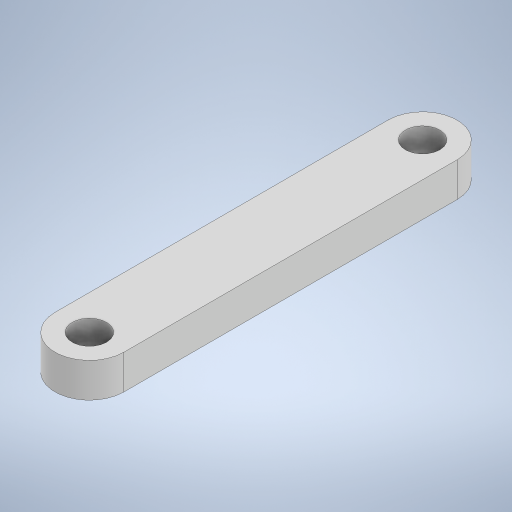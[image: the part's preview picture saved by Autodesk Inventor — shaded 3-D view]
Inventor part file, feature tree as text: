
AUTODESK INVENTOR PART (.ipt)
format: ipt  version: 2023 (Build 270158000, 158)  size: 238,592 bytes
history: native  units: mm
features: extrude x2, sketch x2, other x1
ambient origin geometry x8: Origin, YZ Plane, XZ Plane, XY Plane, X Axis, Y Axis, Z Axis, Center Point
bodies: Body1 (feature_tree)
feature tree (5):
  other  "Sólido1"
  extrude  "Extrusión1"  Depth=6.0mm
  extrude  "Extrusión2"  Depth=3.0mm
  sketch  "Boceto1"  dims[d0=14.5mm d1=6.0mm]
  sketch  "Boceto2"  dims[d2=3.0mm d3=0.0mm d4=3.0mm d5=3.0mm d6=3.0mm d7=0.0mm]
